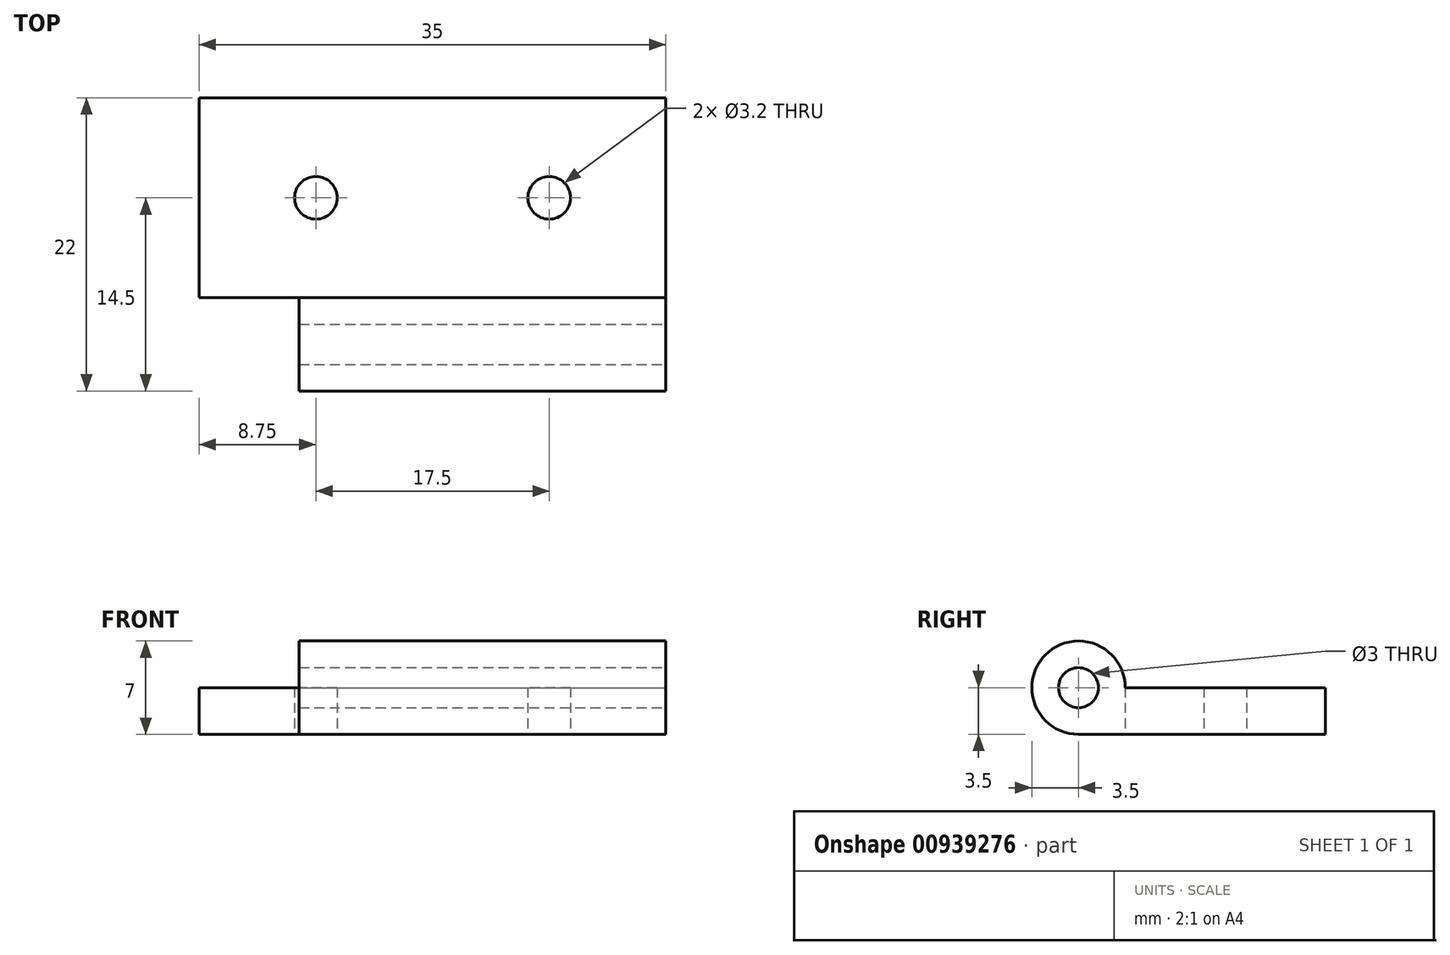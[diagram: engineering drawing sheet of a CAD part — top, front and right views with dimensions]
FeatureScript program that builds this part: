
annotation { "Feature Type Name" : "Feature", "Feature Type Description" : "" }
export const myFeature = defineFeature(function(context is Context, id is Id, definition is map)
    precondition{}
    {
        {
            var Q0;
            Q0=qCreatedBy(makeId("Top.planeOp"),FACE);
            var sketch = newSketch(context, id + "F0", { "sketchPlane" : qUnion([Q0])});
            skLineSegment(sketch, "E0.bottom", {"start": v(-17.5, -7.5) * mm, "end": v(17.5, -7.5) * mm});
            skLineSegment(sketch, "E0.top", {"start": v(-17.5, 7.5) * mm, "end": v(17.5, 7.5) * mm});
            skLineSegment(sketch, "E0.left", {"start": v(-17.5, -7.5) * mm, "end": v(-17.5, 7.5) * mm});
            skLineSegment(sketch, "E0.right", {"start": v(17.5, -7.5) * mm, "end": v(17.5, 7.5) * mm});
            skPoint(sketch, "E0.middle", {"position": v(0, 0) * mm});
            skLineSegment(sketch, "E1", {"start": v(0, 0) * mm, "end": v(-17.5, 0) * mm});
            skLineSegment(sketch, "E2", {"start": v(0, 0) * mm, "end": v(17.5, 0) * mm});
            skCircle(sketch, "E3", {"center": v(-8.75, 0) * mm, "radius": 1.6 * mm});
            skCircle(sketch, "E4", {"center": v(8.75, 0) * mm, "radius": 1.6 * mm});
            skSolve(sketch);
        }
        {
            var Q0;
            {var subQ6=sQuery(id+"F0.wireOp",EDGE,"E0.bottom");Q0=makeQuery(id+"F0.imprint","IMPRINT",FACE,{"disambiguationData":[TD([[makeQuery(id+"F0.imprint","IMPRINT",EDGE,{"derivedFrom":subQ6}),1.0]])]});}
            var Q1;
            {var subQ1=sQuery(id+"F0.wireOp",EDGE,"E0.top");Q1=makeQuery(id+"F0.imprint","IMPRINT",FACE,{"disambiguationData":[TD([[makeQuery(id+"F0.imprint","IMPRINT",EDGE,{"derivedFrom":subQ1}),-1.0]])]});}
            extrude(context, id + "F1", {"entities" : qUnion([Q0, Q1]), "depth" : 3 * mm, "offsetDistance" : 25 * mm});
        }
        {
            var Q0;
            Q0=makeQuery(id+"F1.opExtrude","SWEPT_FACE",FACE,{"disambiguationData":[OSD([sQuery(id+"F0.wireOp",EDGE,"E0.right")])]});
            var sketch = newSketch(context, id + "F2", { "sketchPlane" : qUnion([Q0])});
            skLineSegment(sketch, "E5", {"start": v(-7.5, 3) * mm, "end": v(-11, 3) * mm});
            skCircle(sketch, "E6", {"center": v(-11, 3) * mm, "radius": 1.5 * mm});
            skCircle(sketch, "E7", {"center": v(-11, 3) * mm, "radius": 3.5 * mm});
            skLineSegment(sketch, "E8", {"start": v(7.5, 0) * mm, "end": v(7.5, -0.5) * mm});
            skLineSegment(sketch, "E9", {"start": v(7.5, -0.5) * mm, "end": v(-11, -0.5) * mm});
            skLineSegment(sketch, "E10", {"start": v(-7.5, 0) * mm, "end": v(-7.5, -0.5) * mm});
            skSolve(sketch);
        }
        {
            var Q0;
            Q0=makeQuery(id+"F2.imprint","IMPRINT",FACE,{"disambiguationData":[TD([[makeQuery(id+"F2.imprint","IMPRINT",EDGE,{"derivedFrom":sQuery(id+"F2.wireOp",EDGE,"E6")}),-1.0]])]});
            var Q1;
            {var subQ5=sQuery(id+"F2.wireOp",EDGE,"E10");Q1=makeQuery(id+"F2.imprint","IMPRINT",FACE,{"disambiguationData":[TD([[makeQuery(id+"F2.imprint","IMPRINT",EDGE,{"derivedFrom":subQ5}),-1.0]])]});}
            var Q2;
            {var subQ0=sQuery(id+"F2.wireOp",EDGE,"E8");Q2=makeQuery(id+"F2.imprint","IMPRINT",FACE,{"disambiguationData":[TD([[makeQuery(id+"F2.imprint","IMPRINT",EDGE,{"derivedFrom":subQ0}),-1.0]])]});}
            extrude(context, id + "F3", {"entities" : qUnion([Q0, Q1, Q2]), "operationType" : NewBodyOperationType.ADD, "oppositeDirection" : true, "depth" : 35 * mm, "offsetDistance" : 25 * mm});
        }
        {
            var Q0;
            Q0=makeQuery(id+"F3.boolean.opBoolean","SPLIT",FACE,{"disambiguationData":[TD([makeQuery(id+"F1.opExtrude","SWEPT_FACE",FACE,{"disambiguationData":[OSD([sQuery(id+"F0.wireOp",EDGE,"E3")])]})])],"derivedFrom":makeQuery(id+"F3.opExtrude","SWEPT_FACE",FACE,{"disambiguationData":[OSD([sQuery(id+"F0.wireOp",EDGE,"E0.right")])]})});
            var Q1;
            Q1=makeQuery(id+"F3.boolean.opBoolean","SPLIT",FACE,{"disambiguationData":[TD([makeQuery(id+"F1.opExtrude","SWEPT_FACE",FACE,{"disambiguationData":[OSD([sQuery(id+"F0.wireOp",EDGE,"E4")])]})])],"derivedFrom":makeQuery(id+"F3.opExtrude","SWEPT_FACE",FACE,{"disambiguationData":[OSD([sQuery(id+"F0.wireOp",EDGE,"E0.right")])]})});
            extrude(context, id + "F4", {"entities" : qUnion([Q0, Q1]), "operationType" : NewBodyOperationType.REMOVE, "oppositeDirection" : true, "depth" : 25 * mm, "offsetDistance" : 25 * mm});
        }
        {
            var Q0;
            Q0=makeQuery(id+"F2.imprint","IMPRINT",FACE,{"disambiguationData":[TD([[makeQuery(id+"F2.imprint","IMPRINT",EDGE,{"derivedFrom":sQuery(id+"F2.wireOp",EDGE,"E6")}),-1.0]])]});
            var Q1;
            {var subQ5=sQuery(id+"F2.wireOp",EDGE,"E10");Q1=makeQuery(id+"F2.imprint","IMPRINT",FACE,{"disambiguationData":[TD([[makeQuery(id+"F2.imprint","IMPRINT",EDGE,{"derivedFrom":subQ5}),-1.0]])]});}
            extrude(context, id + "F5", {"entities" : qUnion([Q0, Q1]), "operationType" : NewBodyOperationType.REMOVE, "oppositeDirection" : true, "depth" : 35 * mm, "offsetDistance" : 25 * mm});
        }
        {
            var Q0;
            Q0=makeQuery(id+"F2.imprint","IMPRINT",FACE,{"disambiguationData":[TD([[makeQuery(id+"F2.imprint","IMPRINT",EDGE,{"derivedFrom":sQuery(id+"F2.wireOp",EDGE,"E6")}),-1.0]])]});
            var Q1;
            {var subQ5=sQuery(id+"F2.wireOp",EDGE,"E10");Q1=makeQuery(id+"F2.imprint","IMPRINT",FACE,{"disambiguationData":[TD([[makeQuery(id+"F2.imprint","IMPRINT",EDGE,{"derivedFrom":subQ5}),-1.0]])]});}
            extrude(context, id + "F6", {"entities" : qUnion([Q0, Q1]), "operationType" : NewBodyOperationType.ADD, "oppositeDirection" : true, "depth" : 27.5 * mm, "offsetDistance" : 25 * mm});
        }
    });
